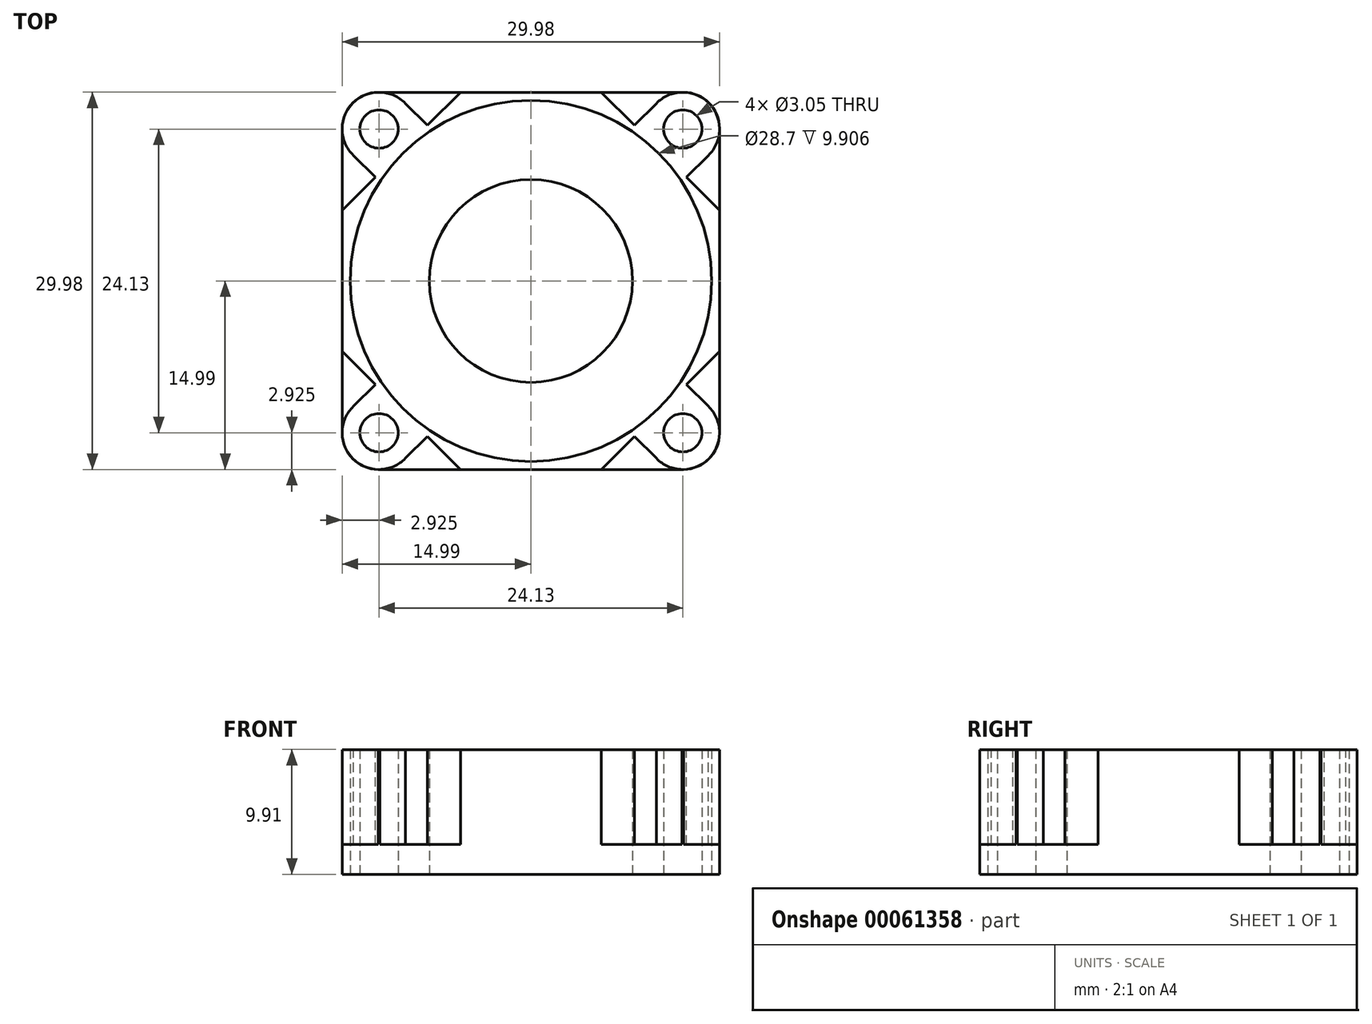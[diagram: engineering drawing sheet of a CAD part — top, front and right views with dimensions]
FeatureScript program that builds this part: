
annotation { "Feature Type Name" : "Feature", "Feature Type Description" : "" }
export const myFeature = defineFeature(function(context is Context, id is Id, definition is map)
    precondition{}
    {
        {
            var Q0;
            Q0=qCreatedBy(makeId("Top.planeOp"),FACE);
            var sketch = newSketch(context, id + "F0", { "sketchPlane" : qUnion([Q0])});
            skLineSegment(sketch, "E0.rect.bottom", {"start": v(-12.12, 14.99) * mm, "end": v(12.12, 14.99) * mm});
            skLineSegment(sketch, "E0.rect.top", {"start": v(-12.12, -14.99) * mm, "end": v(12.12, -14.99) * mm});
            skLineSegment(sketch, "E0.rect.left", {"start": v(-14.99, 12.12) * mm, "end": v(-14.99, -12.12) * mm});
            skLineSegment(sketch, "E0.rect.right", {"start": v(14.99, 12.12) * mm, "end": v(14.99, -12.12) * mm});
            skPoint(sketch, "E0.rect.middle", {"position": v(0, 0) * mm});
            skPoint(sketch, "E1", {"position": v(-12.06, 12.07) * mm});
            skPoint(sketch, "E2", {"position": v(12.07, 12.07) * mm});
            skPoint(sketch, "E3", {"position": v(12.06, -12.07) * mm});
            skPoint(sketch, "E4", {"position": v(-12.07, -12.07) * mm});
            skCircle(sketch, "E5", {"center": v(0, 0) * mm, "radius": 14.35 * mm});
            skPoint(sketch, "E6.visualSharp", {"position": v(-14.99, 14.99) * mm});
            skArc(sketch, "E6.filletArc", {"start": v(-12.12, 14.99) * mm, "mid": v(-14.15, 14.15) * mm, "end": v(-14.99, 12.12) * mm});
            skPoint(sketch, "E7.visualSharp", {"position": v(14.99, 14.99) * mm});
            skArc(sketch, "E7.filletArc", {"start": v(14.99, 12.12) * mm, "mid": v(14.15, 14.15) * mm, "end": v(12.12, 14.99) * mm});
            skPoint(sketch, "E8.visualSharp", {"position": v(14.99, -14.99) * mm});
            skArc(sketch, "E8.filletArc", {"start": v(12.12, -14.99) * mm, "mid": v(14.15, -14.15) * mm, "end": v(14.99, -12.12) * mm});
            skPoint(sketch, "E9.visualSharp", {"position": v(-14.99, -14.99) * mm});
            skArc(sketch, "E9.filletArc", {"start": v(-14.99, -12.12) * mm, "mid": v(-14.15, -14.15) * mm, "end": v(-12.12, -14.99) * mm});
            skSolve(sketch);
        }
        {
            var Q0;
            Q0 = qSketchRegion(id + "F0", true);
            extrude(context, id + "F1", {"entities" : qUnion([Q0]), "depth" : 9.9 * mm});
        }
        {
            var Q0;
            Q0=makeQuery(id+"F1.opExtrude","CAP_FACE",FACE,{"disambiguationData":[OSD([sQuery(id+"F0.wireOp",EDGE,"E0.rect.bottom"),sQuery(id+"F0.wireOp",EDGE,"E0.rect.top"),sQuery(id+"F0.wireOp",EDGE,"E0.rect.left"),sQuery(id+"F0.wireOp",EDGE,"E0.rect.right"),sQuery(id+"F0.wireOp",EDGE,"E5"),sQuery(id+"F0.wireOp",EDGE,"E6.filletArc"),sQuery(id+"F0.wireOp",EDGE,"E7.filletArc"),sQuery(id+"F0.wireOp",EDGE,"E8.filletArc"),sQuery(id+"F0.wireOp",EDGE,"E9.filletArc")])],"isStart":false});
            var sketch = newSketch(context, id + "F2", { "sketchPlane" : qUnion([Q0])});
            skPoint(sketch, "E10.rect.middle", {"position": v(0, 0) * mm});
            skArc(sketch, "E11", {"start": v(-9.96, 14.1) * mm, "mid": v(-14.13, 14.13) * mm, "end": v(-14.1, 9.96) * mm});
            skArc(sketch, "E12", {"start": v(-14.1, -9.96) * mm, "mid": v(-14.13, -14.13) * mm, "end": v(-9.96, -14.1) * mm});
            skArc(sketch, "E13", {"start": v(9.96, -14.1) * mm, "mid": v(14.13, -14.13) * mm, "end": v(14.1, -9.96) * mm});
            skArc(sketch, "E14", {"start": v(14.1, 9.96) * mm, "mid": v(14.13, 14.13) * mm, "end": v(9.96, 14.1) * mm});
            skLineSegment(sketch, "E15.0", {"start": v(10, 14.13) * mm, "end": v(8.23, 12.36) * mm});
            skLineSegment(sketch, "E16.0", {"start": v(14.13, 10) * mm, "end": v(12.36, 8.23) * mm});
            skLineSegment(sketch, "E17.0", {"start": v(-14.13, 10) * mm, "end": v(-12.36, 8.23) * mm});
            skLineSegment(sketch, "E18.0", {"start": v(-10, 14.13) * mm, "end": v(-8.23, 12.36) * mm});
            skLineSegment(sketch, "E19", {"start": v(-5.6, 14.99) * mm, "end": v(5.6, 14.99) * mm});
            skLineSegment(sketch, "E20", {"start": v(14.99, -5.6) * mm, "end": v(14.99, 5.6) * mm});
            skLineSegment(sketch, "E21", {"start": v(-14.99, 5.6) * mm, "end": v(-14.99, -5.6) * mm});
            skLineSegment(sketch, "E22", {"start": v(-5.6, -14.99) * mm, "end": v(5.6, -14.99) * mm});
            skLineSegment(sketch, "E23.trimOffspring", {"start": v(-14.99, -5.6) * mm, "end": v(-12.36, -8.23) * mm});
            skLineSegment(sketch, "E24.trimOffspring", {"start": v(14.99, -5.6) * mm, "end": v(12.36, -8.23) * mm});
            skLineSegment(sketch, "E25.trimOffspring", {"start": v(-12.36, -8.23) * mm, "end": v(-14.13, -10) * mm});
            skLineSegment(sketch, "E26.trimOffspring", {"start": v(-8.23, -12.36) * mm, "end": v(-10, -14.13) * mm});
            skLineSegment(sketch, "E27.trimOffspring", {"start": v(8.23, -12.36) * mm, "end": v(10, -14.13) * mm});
            skLineSegment(sketch, "E28.trimOffspring", {"start": v(12.36, -8.23) * mm, "end": v(14.13, -10) * mm});
            skLineSegment(sketch, "E29.trimOffspring", {"start": v(8.23, -12.36) * mm, "end": v(5.6, -14.99) * mm});
            skLineSegment(sketch, "E30.trimOffspring", {"start": v(12.36, 8.23) * mm, "end": v(14.99, 5.6) * mm});
            skLineSegment(sketch, "E31.trimOffspring", {"start": v(-12.36, 8.23) * mm, "end": v(-14.99, 5.6) * mm});
            skLineSegment(sketch, "E32.trimOffspring", {"start": v(-8.23, -12.36) * mm, "end": v(-5.6, -14.99) * mm});
            skLineSegment(sketch, "E33.trimOffspring", {"start": v(-5.6, 14.99) * mm, "end": v(-8.23, 12.36) * mm});
            skLineSegment(sketch, "E34.trimOffspring", {"start": v(5.6, 14.99) * mm, "end": v(8.23, 12.36) * mm});
            skLineSegment(sketch, "E35.rect.bottom", {"start": v(-17.91, 18.13) * mm, "end": v(17.91, 18.13) * mm});
            skLineSegment(sketch, "E35.rect.top", {"start": v(-17.91, -18.13) * mm, "end": v(17.91, -18.13) * mm});
            skLineSegment(sketch, "E35.rect.left", {"start": v(-17.91, 18.13) * mm, "end": v(-17.91, -18.13) * mm});
            skLineSegment(sketch, "E35.rect.right", {"start": v(17.91, 18.13) * mm, "end": v(17.91, -18.13) * mm});
            skSolve(sketch);
        }
        {
            var Q0;
            Q0 = qSketchRegion(id + "F2", true);
            extrude(context, id + "F3", {"entities" : qUnion([Q0]), "operationType" : NewBodyOperationType.REMOVE, "oppositeDirection" : true, "depth" : 7.54 * mm});
        }
        {
            var Q0;
            Q0=sQuery(id+"F0.wireOp",VERTEX,"E1");
            var Q1;
            Q1=sQuery(id+"F0.wireOp",VERTEX,"E2");
            var Q2;
            Q2=sQuery(id+"F0.wireOp",VERTEX,"E3");
            var Q3;
            Q3=sQuery(id+"F0.wireOp",VERTEX,"E4");
            var Q4;
            Q4=makeQuery(id+"F1.opExtrude","SWEPT_BODY",BODY,{"disambiguationData":[OSD([sQuery(id+"F0.wireOp",EDGE,"E0.rect.bottom"),sQuery(id+"F0.wireOp",EDGE,"E0.rect.top"),sQuery(id+"F0.wireOp",EDGE,"E0.rect.left"),sQuery(id+"F0.wireOp",EDGE,"E0.rect.right"),sQuery(id+"F0.wireOp",EDGE,"E5"),sQuery(id+"F0.wireOp",EDGE,"E6.filletArc"),sQuery(id+"F0.wireOp",EDGE,"E7.filletArc"),sQuery(id+"F0.wireOp",EDGE,"E8.filletArc"),sQuery(id+"F0.wireOp",EDGE,"E9.filletArc")])]});
            hole(context, id + "F4", {"style" : HoleStyle.SIMPLE, "holeDiameter" : 3.05 * mm, "endStyle" : HoleEndStyle.THROUGH, "oppositeDirection" : true, "locations" : qUnion([Q0, Q1, Q2, Q3]), "scope" : qUnion([Q4])});
        }
        {
            var Q0;
            Q0=qCreatedBy(makeId("Top.planeOp"),FACE);
            var sketch = newSketch(context, id + "F5", { "sketchPlane" : qUnion([Q0])});
            skCircle(sketch, "E36", {"center": v(0, 0) * mm, "radius": 8.06 * mm});
            skSolve(sketch);
        }
        {
            var Q0;
            Q0 = qSketchRegion(id + "F5", true);
            extrude(context, id + "F6", {"entities" : qUnion([Q0]), "depth" : 9.9 * mm});
        }
    });
